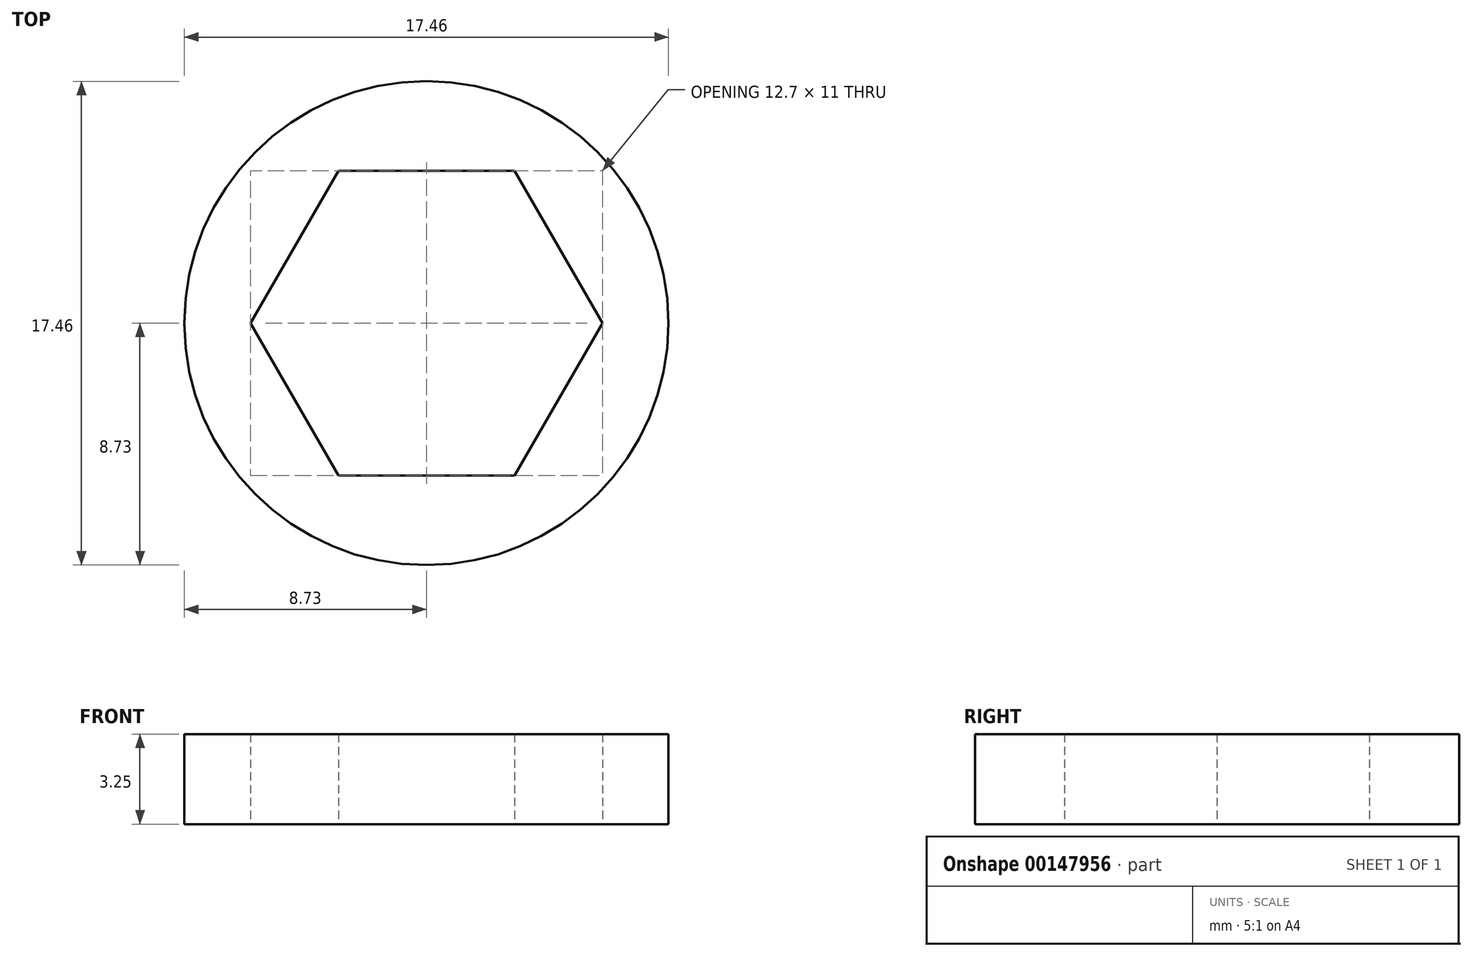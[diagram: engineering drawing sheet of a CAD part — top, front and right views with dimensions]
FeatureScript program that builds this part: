
annotation { "Feature Type Name" : "Feature", "Feature Type Description" : "" }
export const myFeature = defineFeature(function(context is Context, id is Id, definition is map)
    precondition{}
    {
        {
            var Q0;
            Q0=qCreatedBy(makeId("Top.planeOp"),FACE);
            var sketch = newSketch(context, id + "F0", { "sketchPlane" : qUnion([Q0])});
            skCircle(sketch, "E0", {"center": v(0, 0) * mm, "radius": 8.73 * mm});
            skCircle(sketch, "E1.cCircle", {"center": v(0, 0) * mm, "radius": 6.35 * mm, "construction": true});
            skLineSegment(sketch, "E1.0", {"start": v(3.17, -5.5) * mm, "end": v(-3.17, -5.5) * mm});
            skLineSegment(sketch, "E1.1", {"start": v(-3.17, -5.5) * mm, "end": v(-6.35, 0) * mm});
            skLineSegment(sketch, "E1.2", {"start": v(-6.35, 0) * mm, "end": v(-3.18, 5.5) * mm});
            skLineSegment(sketch, "E1.3", {"start": v(-3.18, 5.5) * mm, "end": v(3.17, 5.5) * mm});
            skLineSegment(sketch, "E1.4", {"start": v(3.17, 5.5) * mm, "end": v(6.35, 0) * mm});
            skLineSegment(sketch, "E1.5", {"start": v(6.35, 0) * mm, "end": v(3.17, -5.5) * mm});
            skSolve(sketch);
        }
        {
            var Q0;
            Q0=qSketchRegion(id+"F0",true);
            extrude(context, id + "F1", {"entities" : qUnion([Q0]), "depth" : 3.25 * mm});
        }
    });
